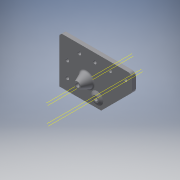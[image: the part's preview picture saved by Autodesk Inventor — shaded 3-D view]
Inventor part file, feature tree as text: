
AUTODESK INVENTOR PART (.ipt)
format: ipt  version: 2018 (Build 220112000, 112)  size: 217,088 bytes
history: native  units: in
note: dims shown in document units (in); Inventor stores cm internally (conversion verified against a paired STEP export)
features: sketch x8, extrude x6, plane x4, revolve x2, fillet x2, projected_geometry x2
ambient origin geometry x8: Origin, YZ Plane, XZ Plane, XY Plane, X Axis, Y Axis, Z Axis, Center Point
bodies: Solid1 (feature_tree)
feature tree (24):
  extrude  "Extrusion1"  Depth=0.7874in
  extrude  "Extrusion2"  Depth=3.5433in
  plane  "Work Plane2"
  revolve  "Revolution1"  [1 undecoded]
  extrude  "Extrusion3"  Depth=0.5118in
  extrude  "Extrusion4"  [1 undecoded]
  fillet  "Fillet1"  Radius=0.3543in
  extrude  "Extrusion5"  TaperAngle=90.0deg  [1 undecoded]
  plane  "Work Plane4"
  revolve  "Revolution2"  [1 undecoded]
  fillet  "Fillet2"  Radius=0.1654in
  extrude  "Extrusion6"  Depth=0.3937in
  sketch  "Sketch1"  dims[d0=0.7874in d1=0.7874in]
  sketch  "Sketch2"  dims[d2=3.5433in d3=3.5433in]
  plane  "Work Plane1"
  sketch  "Sketch3"  dims[d4=0.1969in d5=0.0in d6=0.1969in]
  sketch  "Sketch4"  dims[d7=1.3386in d8=0.5118in]
  projected_geometry  "Projected Loop1"
  sketch  "Sketch5"  dims[d9=0.2362in d10=0.0in d11=-0.0984in d12=0.3543in]
  sketch  "Sketch7"  dims[d13=0.4528in d14=90.0deg]
  plane  "Work Plane3"
  sketch  "Sketch8"  dims[d15=0.2362in d16=0.0in d17=0.1575in d18=0.1654in]
  projected_geometry  "Projected Loop2"
  sketch  "Sketch9"  dims[d19=0.315in d20=0.748in d21=0.748in d22=0.748in d23=0.315in d24=0.748in d25=0.748in d26=0.748in d27=0.2362in d28=0.0in d29=0.0787in d30=0.3268in d32=0.3268in d33=0.1969in d34=0.0in d35=0.0984in d36=0.1969in d37=0.0591in d38=0.0787in d39=90.0deg d40=0.1969in d42=0.3937in d43=0.0in d44=1.2598in]
note: 4 required parameter values undecoded (feature->parameter linkage not recoverable at this tier; creation-order binding heuristic only, values carry confidence <= 0.55)